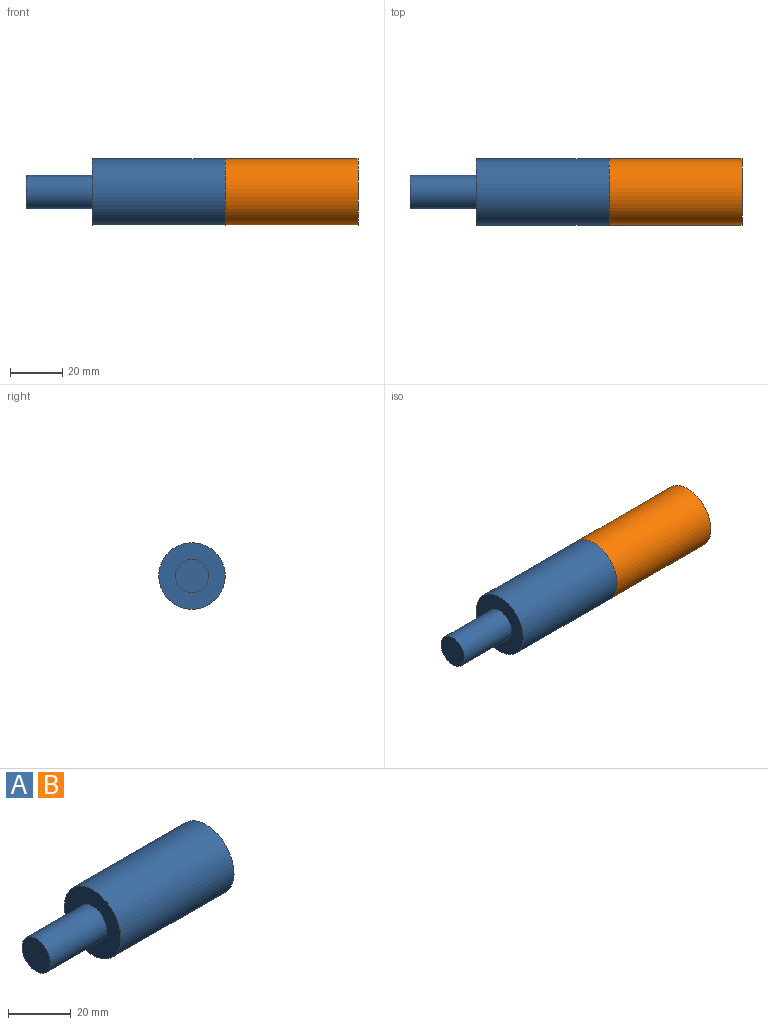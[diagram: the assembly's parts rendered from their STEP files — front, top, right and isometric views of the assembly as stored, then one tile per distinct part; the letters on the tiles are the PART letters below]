
ASSEMBLY  parts=2 mates=1
PART A: 7 faces, bbox 76.2x25.4x25.4 mm
  f0: plane 25.4x25.4mm, normal (-1,0,0), area 380mm2, adj f1,f4
  f1: cylinder r=6.35mm len=25.4mm, axis (-1,0,0), area 1013.4mm2, adj f0,f2
  f2: plane 12.7x12.7mm, normal (-1,0,0), area 126.7mm2, adj f1
  f3: plane 25.4x25.4mm, normal (1,0,0), area 380mm2, adj f4,f6
  f4: cylinder r=12.7mm len=50.8mm, axis (-1,0,0), area 4053.7mm2, adj f0,f3
  f5: cone r=0mm half-angle=59deg, axis (1,0,0), area 147.8mm2, adj f6
  f6: cylinder r=6.35mm len=25.4mm, axis (1,0,0), area 1013.4mm2, adj f3,f5
PART B: same geometry as A
PLACE A t=(72.77,8.89,-32.07)mm
PLACE B t=(123.57,8.89,-32.07)mm
MATE pin_slot B.f1 <-> A.f1  axis (-1,0,0) through (50.54,-28.87,-32.07)mm
